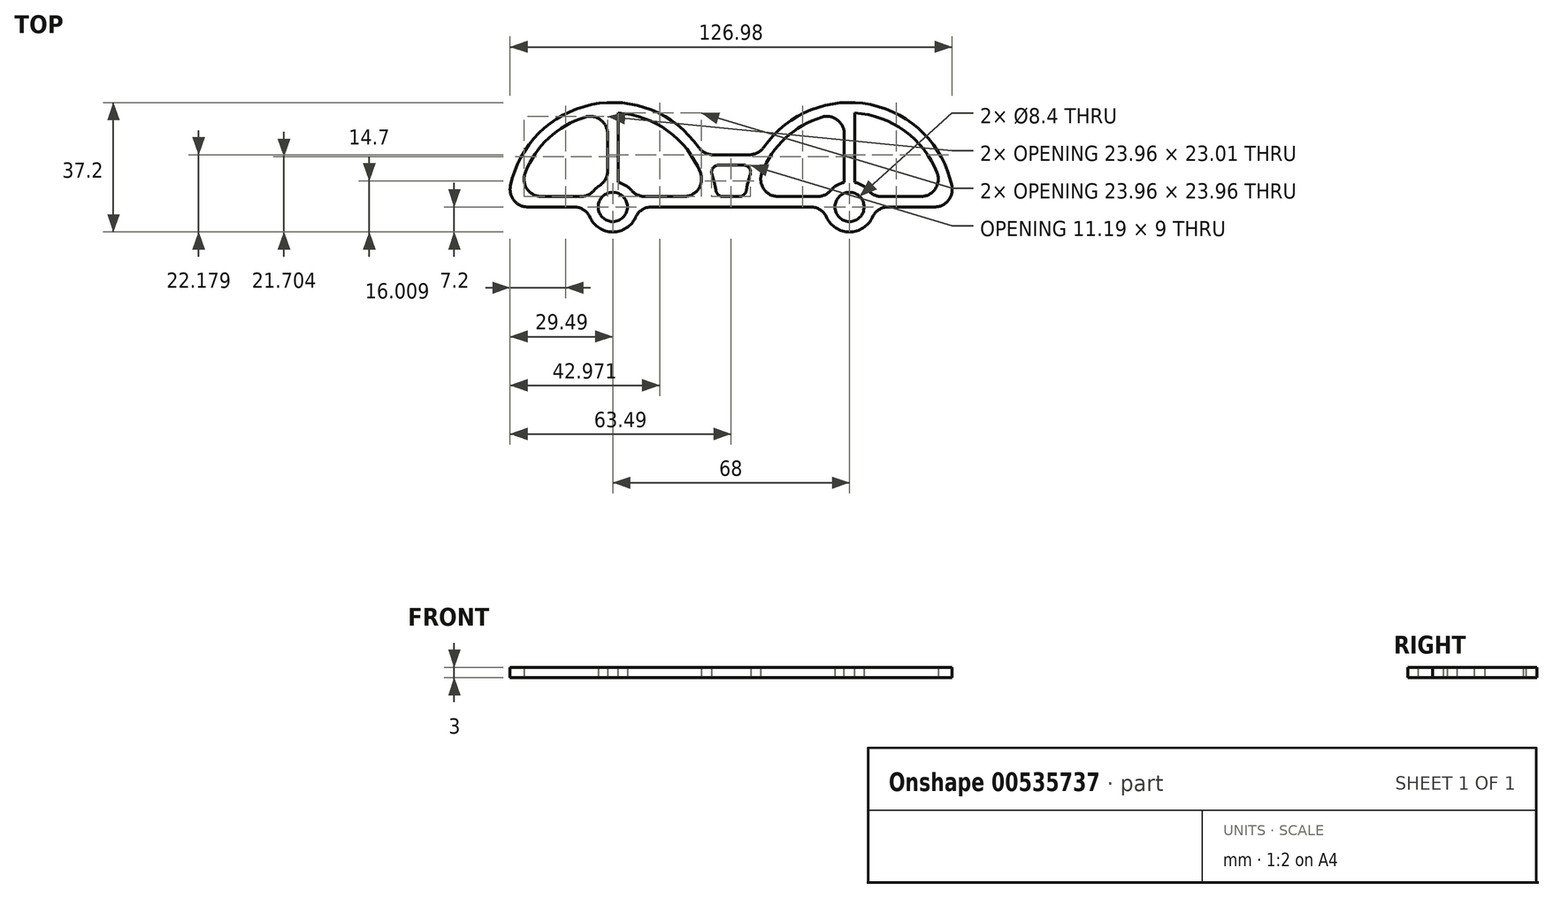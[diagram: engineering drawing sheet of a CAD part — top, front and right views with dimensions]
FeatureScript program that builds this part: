
annotation { "Feature Type Name" : "Feature", "Feature Type Description" : "" }
export const myFeature = defineFeature(function(context is Context, id is Id, definition is map)
    precondition{}
    {
        {
            var Q0;
            Q0=qCreatedBy(makeId("Top.planeOp"),FACE);
            var sketch = newSketch(context, id + "F0", { "sketchPlane" : qUnion([Q0])});
            skCircle(sketch, "E0", {"center": v(0, 0) * mm, "radius": 4.2 * mm});
            skCircle(sketch, "E1", {"center": v(68, 0) * mm, "radius": 4.2 * mm});
            skCircle(sketch, "E2.0", {"center": v(0, 0) * mm, "radius": 7.2 * mm});
            skCircle(sketch, "E3.0", {"center": v(68, 0) * mm, "radius": 7.2 * mm});
            skArc(sketch, "E4", {"start": v(29.85, 3) * mm, "mid": v(29.02, 7.6) * mm, "end": v(27.5, 12) * mm});
            skArc(sketch, "E5", {"start": v(98, 0) * mm, "mid": v(75.76, 28.98) * mm, "end": v(42.02, 15) * mm});
            skLineSegment(sketch, "E6", {"start": v(-7.2, 0) * mm, "end": v(-30, 0) * mm});
            skLineSegment(sketch, "E7", {"start": v(75.2, 0) * mm, "end": v(98, 0) * mm});
            skLineSegment(sketch, "E8", {"start": v(25.98, 15) * mm, "end": v(42.02, 15) * mm});
            skLineSegment(sketch, "E9", {"start": v(7.2, 0) * mm, "end": v(30, 0) * mm});
            skLineSegment(sketch, "E10.trimOffspring", {"start": v(38, 0) * mm, "end": v(60.8, 0) * mm});
            skLineSegment(sketch, "E11", {"start": v(30, 0) * mm, "end": v(38, 0) * mm});
            skArc(sketch, "E12.0", {"start": v(26.83, 3) * mm, "mid": v(0, 27) * mm, "end": v(-26.83, 3) * mm});
            skLineSegment(sketch, "E12.1", {"start": v(6.55, 3) * mm, "end": v(26.83, 3) * mm});
            skLineSegment(sketch, "E12.2", {"start": v(-6.55, 3) * mm, "end": v(-26.83, 3) * mm});
            skArc(sketch, "E13.0", {"start": v(94.83, 3) * mm, "mid": v(68, 27) * mm, "end": v(41.17, 3) * mm});
            skLineSegment(sketch, "E13.1", {"start": v(74.55, 3) * mm, "end": v(94.83, 3) * mm});
            skLineSegment(sketch, "E13.2", {"start": v(41.17, 3) * mm, "end": v(61.45, 3) * mm});
            skLineSegment(sketch, "E14", {"start": v(29.85, 3) * mm, "end": v(38.15, 3) * mm});
            skLineSegment(sketch, "E15.0", {"start": v(27.5, 12) * mm, "end": v(40.5, 12) * mm});
            skArc(sketch, "E16.trimOffspring", {"start": v(40.5, 12) * mm, "mid": v(38.98, 7.6) * mm, "end": v(38.15, 3) * mm});
            skArc(sketch, "E17.trimOffspring", {"start": v(25.98, 15) * mm, "mid": v(-7.76, 28.98) * mm, "end": v(-30, 0) * mm});
            skSolve(sketch);
        }
        {
            var Q0;
            Q0=makeQuery(id+"F0.imprint","IMPRINT",FACE,{"disambiguationData":[TD([[makeQuery(id+"F0.imprint","IMPRINT",EDGE,{"derivedFrom":sQuery(id+"F0.wireOp",EDGE,"E4")}),1.0]])]});
            var Q1;
            Q1=makeQuery(id+"F0.imprint","IMPRINT",FACE,{"disambiguationData":[TD([[makeQuery(id+"F0.imprint","IMPRINT",EDGE,{"derivedFrom":sQuery(id+"F0.wireOp",EDGE,"E0")}),-1.0]])]});
            var Q2;
            Q2=makeQuery(id+"F0.imprint","IMPRINT",FACE,{"disambiguationData":[TD([[makeQuery(id+"F0.imprint","IMPRINT",EDGE,{"derivedFrom":sQuery(id+"F0.wireOp",EDGE,"E1")}),-1.0]])]});
            extrude(context, id + "F1", {"entities" : qUnion([Q0, Q1, Q2]), "depth" : 3 * mm, "offsetDistance" : 25 * mm});
        }
        {
            var Q0;
            Q0=makeQuery(id+"F1.opExtrude","CAP_FACE",FACE,{"disambiguationData":[OSD([sQuery(id+"F0.wireOp",EDGE,"E0"),sQuery(id+"F0.wireOp",EDGE,"E1"),sQuery(id+"F0.wireOp",EDGE,"E2.0"),sQuery(id+"F0.wireOp",EDGE,"E3.0"),sQuery(id+"F0.wireOp",EDGE,"E4"),sQuery(id+"F0.wireOp",EDGE,"E5"),sQuery(id+"F0.wireOp",EDGE,"E6"),sQuery(id+"F0.wireOp",EDGE,"E7"),sQuery(id+"F0.wireOp",EDGE,"E8"),sQuery(id+"F0.wireOp",EDGE,"E9"),sQuery(id+"F0.wireOp",EDGE,"E10.trimOffspring"),sQuery(id+"F0.wireOp",EDGE,"E11"),sQuery(id+"F0.wireOp",EDGE,"E12.0"),sQuery(id+"F0.wireOp",EDGE,"E12.1"),sQuery(id+"F0.wireOp",EDGE,"E12.2"),sQuery(id+"F0.wireOp",EDGE,"E13.0"),sQuery(id+"F0.wireOp",EDGE,"E13.1"),sQuery(id+"F0.wireOp",EDGE,"E13.2"),sQuery(id+"F0.wireOp",EDGE,"E14"),sQuery(id+"F0.wireOp",EDGE,"E15.0"),sQuery(id+"F0.wireOp",EDGE,"E16.trimOffspring"),sQuery(id+"F0.wireOp",EDGE,"E17.trimOffspring")])],"isStart":false});
            var sketch = newSketch(context, id + "F2", { "sketchPlane" : qUnion([Q0])});
            skLineSegment(sketch, "E18.0.0", {"start": v(-30, 0) * mm, "end": v(-7.2, 0) * mm});
            skArc(sketch, "E18.0.1", {"start": v(-7.2, 0) * mm, "mid": v(0, -7.2) * mm, "end": v(7.2, 0) * mm});
            skLineSegment(sketch, "E18.0.2", {"start": v(7.2, 0) * mm, "end": v(60.8, 0) * mm});
            skArc(sketch, "E18.0.3", {"start": v(60.8, 0) * mm, "mid": v(68, -7.2) * mm, "end": v(75.2, 0) * mm});
            skLineSegment(sketch, "E18.0.4", {"start": v(75.2, 0) * mm, "end": v(98, 0) * mm});
            skArc(sketch, "E18.0.5", {"start": v(98, 0) * mm, "mid": v(75.76, 28.98) * mm, "end": v(42.02, 15) * mm});
            skLineSegment(sketch, "E18.0.6", {"start": v(42.02, 15) * mm, "end": v(25.98, 15) * mm});
            skArc(sketch, "E18.0.7", {"start": v(25.98, 15) * mm, "mid": v(-7.76, 28.98) * mm, "end": v(-30, 0) * mm});
            skArc(sketch, "E19.0", {"start": v(26.83, 3) * mm, "mid": v(0, 27) * mm, "end": v(-26.83, 3) * mm});
            skLineSegment(sketch, "E20.0", {"start": v(6.55, 3) * mm, "end": v(26.83, 3) * mm});
            skArc(sketch, "E21.0", {"start": v(6.55, 3) * mm, "mid": v(0, 7.2) * mm, "end": v(-6.55, 3) * mm});
            skLineSegment(sketch, "E22.0", {"start": v(-6.55, 3) * mm, "end": v(-26.83, 3) * mm});
            skArc(sketch, "E23.0", {"start": v(94.83, 3) * mm, "mid": v(68, 27) * mm, "end": v(41.17, 3) * mm});
            skLineSegment(sketch, "E24.0", {"start": v(41.17, 3) * mm, "end": v(61.45, 3) * mm});
            skLineSegment(sketch, "E25.0", {"start": v(74.55, 3) * mm, "end": v(94.83, 3) * mm});
            skArc(sketch, "E26.0", {"start": v(74.55, 3) * mm, "mid": v(68, 7.2) * mm, "end": v(61.45, 3) * mm});
            skLineSegment(sketch, "E27", {"start": v(0, 7.2) * mm, "end": v(0, 27) * mm});
            skLineSegment(sketch, "E28", {"start": v(68, 7.2) * mm, "end": v(68, 27) * mm});
            skLineSegment(sketch, "E29.0", {"start": v(69.5, 7.04) * mm, "end": v(69.5, 26.96) * mm});
            skLineSegment(sketch, "E30.0", {"start": v(66.5, 7.04) * mm, "end": v(66.5, 26.96) * mm});
            skLineSegment(sketch, "E31.0", {"start": v(-1.5, 7.04) * mm, "end": v(-1.5, 26.96) * mm});
            skLineSegment(sketch, "E32.0", {"start": v(1.5, 7.04) * mm, "end": v(1.5, 26.96) * mm});
            skSolve(sketch);
        }
        {
            var Q0;
            {var subQ0=sQuery(id+"F2.wireOp",EDGE,"E27");Q0=makeQuery(id+"F2.imprint","IMPRINT",FACE,{"disambiguationData":[TD([[makeQuery(id+"F2.imprint","IMPRINT",EDGE,{"derivedFrom":subQ0}),-1.0]])]});}
            var Q1;
            {var subQ0=sQuery(id+"F2.wireOp",EDGE,"E27");Q1=makeQuery(id+"F2.imprint","IMPRINT",FACE,{"disambiguationData":[TD([[makeQuery(id+"F2.imprint","IMPRINT",EDGE,{"derivedFrom":subQ0}),1.0]])]});}
            var Q2;
            {var subQ0=sQuery(id+"F2.wireOp",EDGE,"E28");Q2=makeQuery(id+"F2.imprint","IMPRINT",FACE,{"disambiguationData":[TD([[makeQuery(id+"F2.imprint","IMPRINT",EDGE,{"derivedFrom":subQ0}),1.0]])]});}
            var Q3;
            {var subQ0=sQuery(id+"F2.wireOp",EDGE,"E28");Q3=makeQuery(id+"F2.imprint","IMPRINT",FACE,{"disambiguationData":[TD([[makeQuery(id+"F2.imprint","IMPRINT",EDGE,{"derivedFrom":subQ0}),-1.0]])]});}
            var Q4;
            Q4=makeQuery(id+"F1.opExtrude","CAP_FACE",FACE,{"disambiguationData":[OSD([sQuery(id+"F0.wireOp",EDGE,"E0"),sQuery(id+"F0.wireOp",EDGE,"E1"),sQuery(id+"F0.wireOp",EDGE,"E2.0"),sQuery(id+"F0.wireOp",EDGE,"E3.0"),sQuery(id+"F0.wireOp",EDGE,"E4"),sQuery(id+"F0.wireOp",EDGE,"E5"),sQuery(id+"F0.wireOp",EDGE,"E6"),sQuery(id+"F0.wireOp",EDGE,"E7"),sQuery(id+"F0.wireOp",EDGE,"E8"),sQuery(id+"F0.wireOp",EDGE,"E9"),sQuery(id+"F0.wireOp",EDGE,"E10.trimOffspring"),sQuery(id+"F0.wireOp",EDGE,"E11"),sQuery(id+"F0.wireOp",EDGE,"E12.0"),sQuery(id+"F0.wireOp",EDGE,"E12.1"),sQuery(id+"F0.wireOp",EDGE,"E12.2"),sQuery(id+"F0.wireOp",EDGE,"E13.0"),sQuery(id+"F0.wireOp",EDGE,"E13.1"),sQuery(id+"F0.wireOp",EDGE,"E13.2"),sQuery(id+"F0.wireOp",EDGE,"E14"),sQuery(id+"F0.wireOp",EDGE,"E15.0"),sQuery(id+"F0.wireOp",EDGE,"E16.trimOffspring"),sQuery(id+"F0.wireOp",EDGE,"E17.trimOffspring")])],"isStart":true});
            extrude(context, id + "F3", {"entities" : qUnion([Q0, Q1, Q2, Q3]), "operationType" : NewBodyOperationType.ADD, "endBound" : BoundingType.UP_TO_SURFACE, "oppositeDirection" : true, "depth" : 25 * mm, "endBoundEntityFace" : qUnion([Q4]), "offsetDistance" : 25 * mm});
        }
        {
            var Q0;
            Q0=makeQuery(id+"F1.opExtrude","SWEPT_EDGE",EDGE,{"disambiguationData":[OSD([sQuery(id+"F0.wireOp",EDGE,"E12.0"),sQuery(id+"F0.wireOp",EDGE,"E12.2")])]});
            var Q1;
            Q1=makeQuery(id+"F1.opExtrude","SWEPT_EDGE",EDGE,{"disambiguationData":[OSD([sQuery(id+"F0.wireOp",EDGE,"E12.0"),sQuery(id+"F0.wireOp",EDGE,"E12.1")])]});
            var Q2;
            Q2=makeQuery(id+"F1.opExtrude","SWEPT_EDGE",EDGE,{"disambiguationData":[OSD([sQuery(id+"F0.wireOp",EDGE,"E13.0"),sQuery(id+"F0.wireOp",EDGE,"E13.1")])]});
            var Q3;
            Q3=makeQuery(id+"F1.opExtrude","SWEPT_EDGE",EDGE,{"disambiguationData":[OSD([sQuery(id+"F0.wireOp",EDGE,"E13.0"),sQuery(id+"F0.wireOp",EDGE,"E13.2")])]});
            var Q4;
            Q4=makeQuery(id+"F1.opExtrude","SWEPT_EDGE",EDGE,{"disambiguationData":[OSD([sQuery(id+"F0.wireOp",EDGE,"E2.0"),sQuery(id+"F0.wireOp",EDGE,"E6")])]});
            var Q5;
            Q5=makeQuery(id+"F1.opExtrude","SWEPT_EDGE",EDGE,{"disambiguationData":[OSD([sQuery(id+"F0.wireOp",EDGE,"E2.0"),sQuery(id+"F0.wireOp",EDGE,"E9")])]});
            var Q6;
            Q6=makeQuery(id+"F1.opExtrude","SWEPT_EDGE",EDGE,{"disambiguationData":[OSD([sQuery(id+"F0.wireOp",EDGE,"E3.0"),sQuery(id+"F0.wireOp",EDGE,"E10.trimOffspring")])]});
            var Q7;
            Q7=makeQuery(id+"F1.opExtrude","SWEPT_EDGE",EDGE,{"disambiguationData":[OSD([sQuery(id+"F0.wireOp",EDGE,"E3.0"),sQuery(id+"F0.wireOp",EDGE,"E7")])]});
            var Q8;
            Q8=makeQuery(id+"F1.opExtrude","SWEPT_EDGE",EDGE,{"disambiguationData":[OSD([sQuery(id+"F0.wireOp",EDGE,"E3.0"),sQuery(id+"F0.wireOp",EDGE,"E13.1")])]});
            var Q9;
            Q9=makeQuery(id+"F1.opExtrude","SWEPT_EDGE",EDGE,{"disambiguationData":[OSD([sQuery(id+"F0.wireOp",EDGE,"E3.0"),sQuery(id+"F0.wireOp",EDGE,"E13.2")])]});
            var Q10;
            Q10=makeQuery(id+"F1.opExtrude","SWEPT_EDGE",EDGE,{"disambiguationData":[OSD([sQuery(id+"F0.wireOp",EDGE,"E2.0"),sQuery(id+"F0.wireOp",EDGE,"E12.2")])]});
            var Q11;
            Q11=makeQuery(id+"F1.opExtrude","SWEPT_EDGE",EDGE,{"disambiguationData":[OSD([sQuery(id+"F0.wireOp",EDGE,"E2.0"),sQuery(id+"F0.wireOp",EDGE,"E12.1")])]});
            var Q12;
            Q12=makeQuery(id+"F1.opExtrude","SWEPT_EDGE",EDGE,{"disambiguationData":[OSD([sQuery(id+"F0.wireOp",EDGE,"E8"),sQuery(id+"F0.wireOp",EDGE,"E17.trimOffspring")])]});
            var Q13;
            Q13=makeQuery(id+"F1.opExtrude","SWEPT_EDGE",EDGE,{"disambiguationData":[OSD([sQuery(id+"F0.wireOp",EDGE,"E5"),sQuery(id+"F0.wireOp",EDGE,"E8")])]});
            var Q14;
            Q14=makeQuery(id+"F1.opExtrude","SWEPT_EDGE",EDGE,{"disambiguationData":[OSD([sQuery(id+"F0.wireOp",EDGE,"E5"),sQuery(id+"F0.wireOp",EDGE,"E7")])]});
            var Q15;
            Q15=makeQuery(id+"F1.opExtrude","SWEPT_EDGE",EDGE,{"disambiguationData":[OSD([sQuery(id+"F0.wireOp",EDGE,"E6"),sQuery(id+"F0.wireOp",EDGE,"E17.trimOffspring")])]});
            var Q16;
            Q16=makeQuery(id+"F3.opExtrude","SWEPT_EDGE",EDGE,{"disambiguationData":[OSD([sQuery(id+"F2.wireOp",EDGE,"E21.0"),sQuery(id+"F2.wireOp",EDGE,"E31.0")])]});
            var Q17;
            Q17=makeQuery(id+"F3.opExtrude","SWEPT_EDGE",EDGE,{"disambiguationData":[OSD([sQuery(id+"F2.wireOp",EDGE,"E21.0"),sQuery(id+"F2.wireOp",EDGE,"E32.0")])]});
            var Q18;
            Q18=makeQuery(id+"F3.opExtrude","SWEPT_EDGE",EDGE,{"disambiguationData":[OSD([sQuery(id+"F2.wireOp",EDGE,"E19.0"),sQuery(id+"F2.wireOp",EDGE,"E32.0")])]});
            var Q19;
            Q19=makeQuery(id+"F3.opExtrude","SWEPT_EDGE",EDGE,{"disambiguationData":[OSD([sQuery(id+"F2.wireOp",EDGE,"E19.0"),sQuery(id+"F2.wireOp",EDGE,"E31.0")])]});
            var Q20;
            Q20=makeQuery(id+"F3.opExtrude","SWEPT_EDGE",EDGE,{"disambiguationData":[OSD([sQuery(id+"F2.wireOp",EDGE,"E23.0"),sQuery(id+"F2.wireOp",EDGE,"E29.0")])]});
            var Q21;
            Q21=makeQuery(id+"F3.opExtrude","SWEPT_EDGE",EDGE,{"disambiguationData":[OSD([sQuery(id+"F2.wireOp",EDGE,"E23.0"),sQuery(id+"F2.wireOp",EDGE,"E30.0")])]});
            fillet(context, id + "F4", {"entities" : qUnion([Q0, Q1, Q2, Q3, Q4, Q5, Q6, Q7, Q8, Q9, Q10, Q11, Q12, Q13, Q14, Q15, Q16, Q17, Q18, Q19, Q20, Q21]), "radius" : 5 * mm, "tangentPropagation" : true, "allowEdgeOverflow" : false});
        }
        {
            var Q0;
            Q0=makeQuery(id+"F1.opExtrude","SWEPT_EDGE",EDGE,{"disambiguationData":[OSD([sQuery(id+"F0.wireOp",EDGE,"E4"),sQuery(id+"F0.wireOp",EDGE,"E15.0")])]});
            var Q1;
            Q1=makeQuery(id+"F1.opExtrude","SWEPT_EDGE",EDGE,{"disambiguationData":[OSD([sQuery(id+"F0.wireOp",EDGE,"E15.0"),sQuery(id+"F0.wireOp",EDGE,"E16.trimOffspring")])]});
            var Q2;
            Q2=makeQuery(id+"F1.opExtrude","SWEPT_EDGE",EDGE,{"disambiguationData":[OSD([sQuery(id+"F0.wireOp",EDGE,"E4"),sQuery(id+"F0.wireOp",EDGE,"E14")])]});
            var Q3;
            Q3=makeQuery(id+"F1.opExtrude","SWEPT_EDGE",EDGE,{"disambiguationData":[OSD([sQuery(id+"F0.wireOp",EDGE,"E14"),sQuery(id+"F0.wireOp",EDGE,"E16.trimOffspring")])]});
            fillet(context, id + "F5", {"entities" : qUnion([Q0, Q1, Q2, Q3]), "radius" : 2 * mm, "tangentPropagation" : true, "allowEdgeOverflow" : false});
        }
    });
